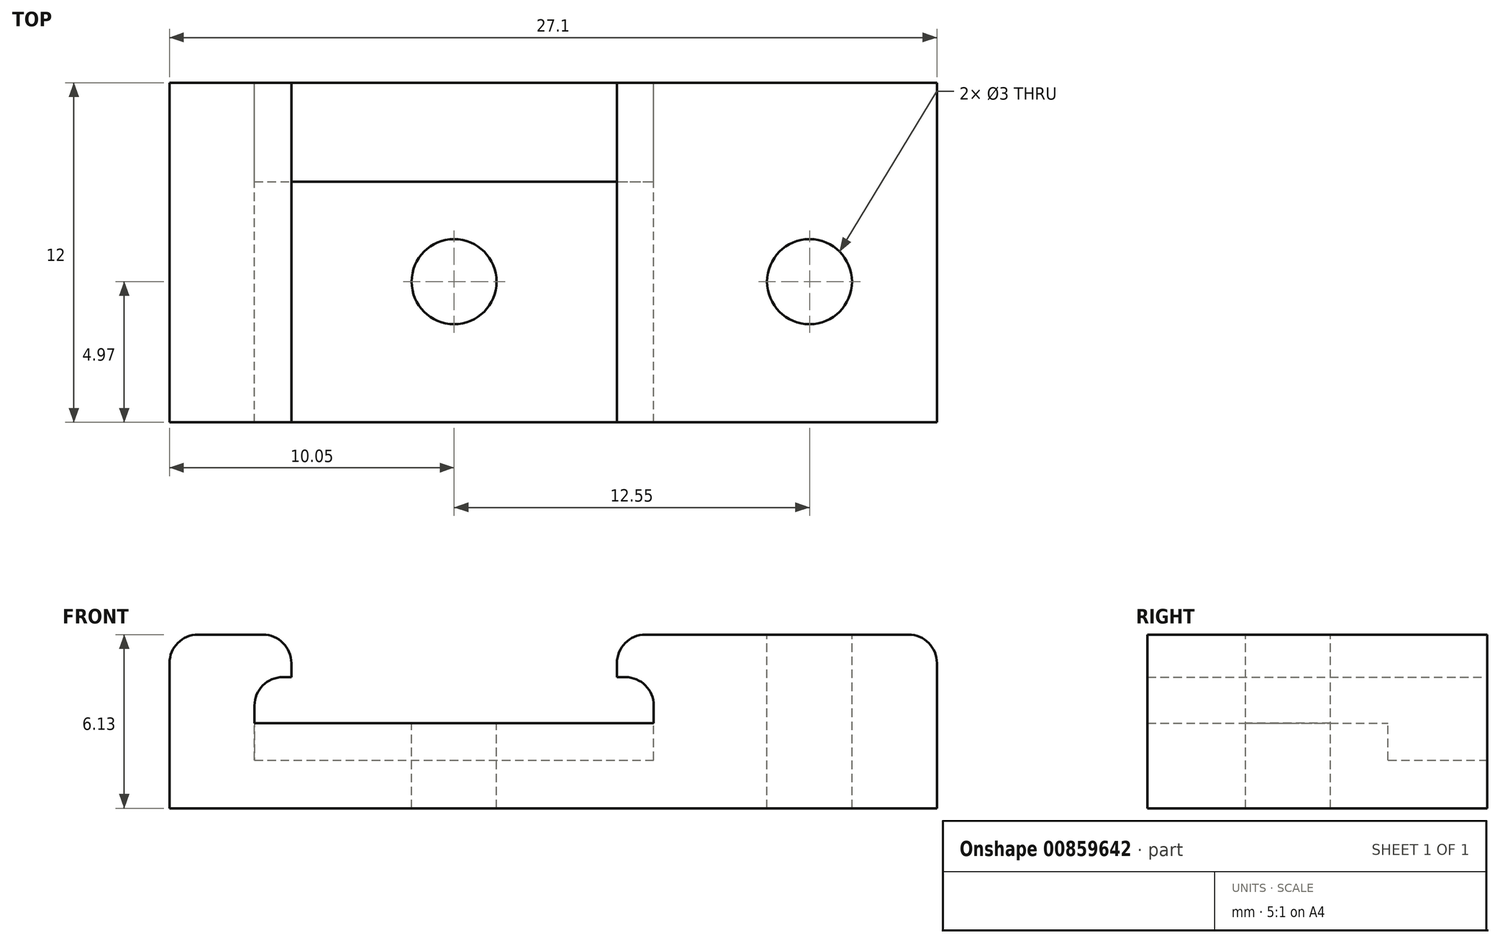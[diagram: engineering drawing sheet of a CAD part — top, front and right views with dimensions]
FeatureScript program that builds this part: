
annotation { "Feature Type Name" : "Feature", "Feature Type Description" : "" }
export const myFeature = defineFeature(function(context is Context, id is Id, definition is map)
    precondition{}
    {
        {
            var Q0;
            Q0=qCreatedBy(makeId("Front.planeOp"),FACE);
            var sketch = newSketch(context, id + "F0", { "sketchPlane" : qUnion([Q0])});
            skLineSegment(sketch, "E0", {"start": v(0, 0) * mm, "end": v(-27.1, 0) * mm});
            skLineSegment(sketch, "E1", {"start": v(-27.1, 0) * mm, "end": v(-27.1, 6.13) * mm});
            skLineSegment(sketch, "E2", {"start": v(-27.1, 6.13) * mm, "end": v(-22.8, 6.13) * mm});
            skLineSegment(sketch, "E3", {"start": v(-22.8, 6.13) * mm, "end": v(-22.8, 4.63) * mm});
            skLineSegment(sketch, "E4", {"start": v(-22.8, 4.63) * mm, "end": v(-24.1, 4.63) * mm});
            skLineSegment(sketch, "E5", {"start": v(-24.1, 4.63) * mm, "end": v(-24.1, 3) * mm});
            skLineSegment(sketch, "E6", {"start": v(-24.1, 3) * mm, "end": v(-10, 3) * mm});
            skLineSegment(sketch, "E7", {"start": v(-10, 3) * mm, "end": v(-10, 4.63) * mm});
            skLineSegment(sketch, "E8", {"start": v(-10, 4.63) * mm, "end": v(-11.3, 4.63) * mm});
            skLineSegment(sketch, "E9", {"start": v(-11.3, 4.63) * mm, "end": v(-11.3, 6.13) * mm});
            skLineSegment(sketch, "E10", {"start": v(-11.3, 6.13) * mm, "end": v(0, 6.13) * mm});
            skLineSegment(sketch, "E11", {"start": v(0, 6.13) * mm, "end": v(0, 0) * mm});
            skSolve(sketch);
        }
        {
            var Q0;
            Q0=makeQuery(id+"F0.imprint","IMPRINT",FACE,{"disambiguationData":[TD([[makeQuery(id+"F0.imprint","IMPRINT",EDGE,{"derivedFrom":sQuery(id+"F0.wireOp",EDGE,"E0")}),-1.0]])]});
            extrude(context, id + "F1", {"entities" : qUnion([Q0]), "depth" : 12 * mm, "offsetDistance" : 25 * mm});
        }
        {
            var Q0;
            Q0=makeQuery(id+"F1.opExtrude","SWEPT_FACE",FACE,{"disambiguationData":[OSD([sQuery(id+"F0.wireOp",EDGE,"E6")])]});
            var sketch = newSketch(context, id + "F2", { "sketchPlane" : qUnion([Q0])});
            skLineSegment(sketch, "E12.bottom", {"start": v(-24.1, 0) * mm, "end": v(-10, 0) * mm});
            skLineSegment(sketch, "E12.top", {"start": v(-24.1, -3.5) * mm, "end": v(-10, -3.5) * mm});
            skLineSegment(sketch, "E12.left", {"start": v(-24.1, 0) * mm, "end": v(-24.1, -3.5) * mm});
            skLineSegment(sketch, "E12.right", {"start": v(-10, 0) * mm, "end": v(-10, -3.5) * mm});
            skSolve(sketch);
        }
        {
            var Q0;
            Q0=makeQuery(id+"F2.imprint","IMPRINT",FACE,{"disambiguationData":[TD([[makeQuery(id+"F2.imprint","IMPRINT",EDGE,{"derivedFrom":sQuery(id+"F2.wireOp",EDGE,"E12.bottom")}),-1.0]])]});
            extrude(context, id + "F3", {"entities" : qUnion([Q0]), "operationType" : NewBodyOperationType.REMOVE, "oppositeDirection" : true, "depth" : 1.3 * mm, "offsetDistance" : 25 * mm});
        }
        {
            var Q0;
            Q0=makeQuery(id+"F1.opExtrude","SWEPT_FACE",FACE,{"disambiguationData":[OSD([sQuery(id+"F0.wireOp",EDGE,"E6")])]});
            var sketch = newSketch(context, id + "F4", { "sketchPlane" : qUnion([Q0])});
            skCircle(sketch, "E13", {"center": v(-17.05, -7.03) * mm, "radius": 1.5 * mm});
            skSolve(sketch);
        }
        {
            var Q0;
            Q0=makeQuery(id+"F4.imprint","IMPRINT",FACE,{"disambiguationData":[TD([[makeQuery(id+"F4.imprint","IMPRINT",EDGE,{"derivedFrom":sQuery(id+"F4.wireOp",EDGE,"E13")}),1.0]])]});
            extrude(context, id + "F5", {"entities" : qUnion([Q0]), "operationType" : NewBodyOperationType.REMOVE, "endBound" : BoundingType.UP_TO_NEXT, "oppositeDirection" : true, "depth" : 25 * mm, "offsetDistance" : 25 * mm});
        }
        {
            var Q0;
            Q0=makeQuery(id+"F1.opExtrude","SWEPT_FACE",FACE,{"disambiguationData":[OSD([sQuery(id+"F0.wireOp",EDGE,"E10")])]});
            var sketch = newSketch(context, id + "F6", { "sketchPlane" : qUnion([Q0])});
            skCircle(sketch, "E14", {"center": v(-4.5, -7.03) * mm, "radius": 1.5 * mm});
            skCircle(sketch, "E15.0", {"center": v(-17.05, -7.03) * mm, "radius": 1.5 * mm, "construction": true});
            skLineSegment(sketch, "E16", {"start": v(-4.5, -7.03) * mm, "end": v(-4.5, -12) * mm, "construction": true});
            skLineSegment(sketch, "E17.0", {"start": v(-24.1, -12) * mm, "end": v(-10, -12) * mm, "construction": true});
            skLineSegment(sketch, "E18", {"start": v(-17.05, -12) * mm, "end": v(-17.05, -7.03) * mm, "construction": true});
            skSolve(sketch);
        }
        {
            var Q0;
            Q0=makeQuery(id+"F6.imprint","IMPRINT",FACE,{"disambiguationData":[TD([[makeQuery(id+"F6.imprint","IMPRINT",EDGE,{"derivedFrom":sQuery(id+"F6.wireOp",EDGE,"E14")}),1.0]])]});
            extrude(context, id + "F7", {"entities" : qUnion([Q0]), "operationType" : NewBodyOperationType.REMOVE, "endBound" : BoundingType.UP_TO_NEXT, "oppositeDirection" : true, "depth" : 25 * mm, "offsetDistance" : 25 * mm});
        }
        {
            var Q0;
            Q0=makeQuery(id+"F1.opExtrude","SWEPT_EDGE",EDGE,{"disambiguationData":[OSD([sQuery(id+"F0.wireOp",EDGE,"E2"),sQuery(id+"F0.wireOp",EDGE,"E3")])]});
            var Q1;
            Q1=makeQuery(id+"F1.opExtrude","SWEPT_EDGE",EDGE,{"disambiguationData":[OSD([sQuery(id+"F0.wireOp",EDGE,"E9"),sQuery(id+"F0.wireOp",EDGE,"E10")])]});
            var Q2;
            Q2=makeQuery(id+"F1.opExtrude","SWEPT_EDGE",EDGE,{"disambiguationData":[OSD([sQuery(id+"F0.wireOp",EDGE,"E1"),sQuery(id+"F0.wireOp",EDGE,"E2")])]});
            var Q3;
            Q3=makeQuery(id+"F1.opExtrude","SWEPT_EDGE",EDGE,{"disambiguationData":[OSD([sQuery(id+"F0.wireOp",EDGE,"E10"),sQuery(id+"F0.wireOp",EDGE,"E11")])]});
            var Q4;
            Q4=makeQuery(id+"F3.boolean.opBoolean","COPY",EDGE,{"derivedFrom":makeQuery(id+"F3.opExtrude","CAP_EDGE",EDGE,{"disambiguationData":[OSD([sQuery(id+"F2.wireOp",EDGE,"E12.top")])],"isStart":true})});
            fillet(context, id + "F8", {"entities" : qUnion([Q0, Q1, Q2, Q3, Q4]), "radius" : 1 * mm, "tangentPropagation" : true, "allowEdgeOverflow" : false});
        }
        {
            var Q0;
            Q0=makeQuery(id+"F1.opExtrude","SWEPT_EDGE",EDGE,{"disambiguationData":[OSD([sQuery(id+"F0.wireOp",EDGE,"E4"),sQuery(id+"F0.wireOp",EDGE,"E5")])]});
            var Q1;
            Q1=makeQuery(id+"F1.opExtrude","SWEPT_EDGE",EDGE,{"disambiguationData":[OSD([sQuery(id+"F0.wireOp",EDGE,"E7"),sQuery(id+"F0.wireOp",EDGE,"E8")])]});
            fillet(context, id + "F9", {"entities" : qUnion([Q0, Q1]), "radius" : 1 * mm, "tangentPropagation" : true, "allowEdgeOverflow" : false});
        }
    });
